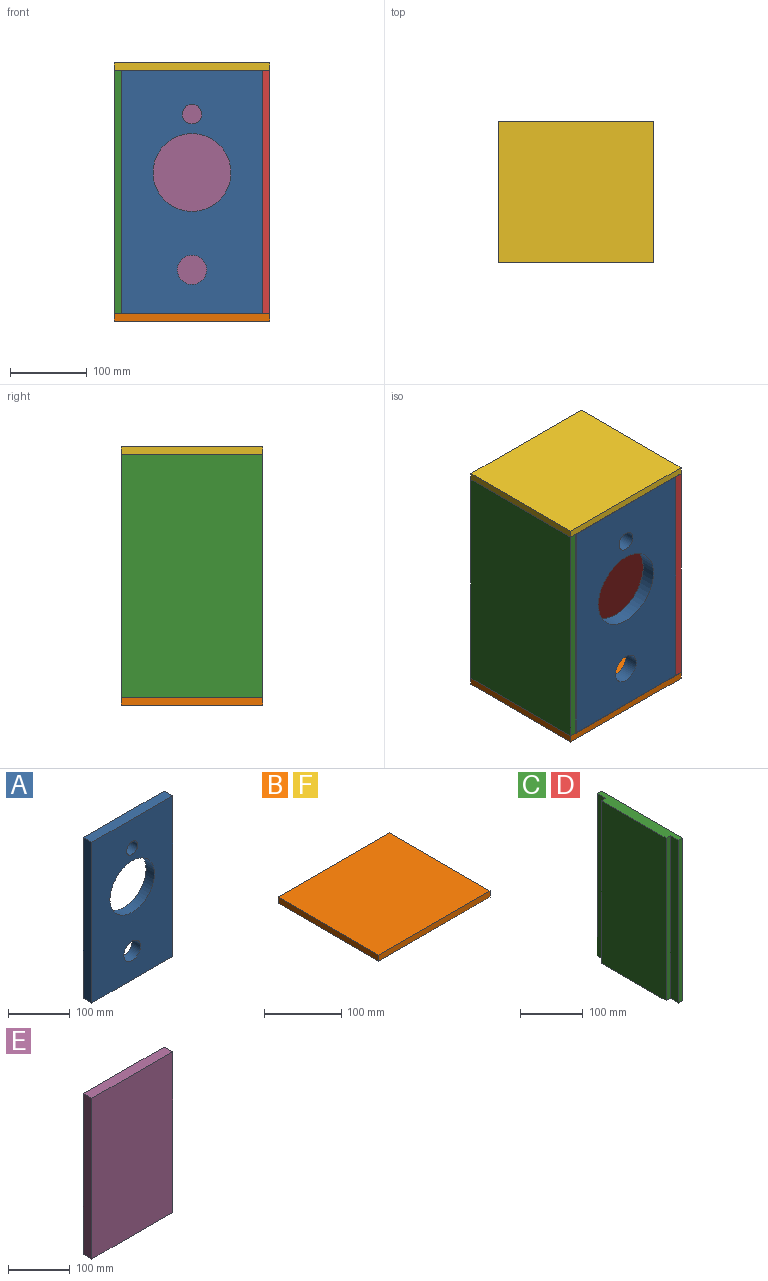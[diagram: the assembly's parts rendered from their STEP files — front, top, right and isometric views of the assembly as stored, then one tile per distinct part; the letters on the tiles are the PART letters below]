
ASSEMBLY  parts=6 mates=5
PART A: 9 faces, bbox 184.2x19.1x317.5 mm
  f0: plane 184.15x19.05mm, normal (0,0,-1), area 3508.1mm2, adj f1,f6,f7,f8
  f1: plane 317.5x19.05mm, normal (1,0,0), area 6048.4mm2, adj f0,f2,f7,f8
  f2: plane 184.15x19.05mm, normal (0,0,1), area 3508.1mm2, adj f1,f6,f7,f8
  f3: cylinder r=50.8mm len=101.6mm, axis (0,1,0), area 6080.5mm2, adj f7,f8
  f4: cylinder r=12.7mm len=25.4mm, axis (0,1,0), area 1520.1mm2, adj f7,f8
  f5: cylinder r=19.05mm len=38.1mm, axis (0,1,0), area 2280.2mm2, adj f7,f8
  f6: plane 317.5x19.05mm, normal (-1,0,0), area 6048.4mm2, adj f0,f2,f7,f8
  f7: plane 317.5x184.15mm, normal (0,-1,0), area 48713.5mm2, adj f0,f1,f2,f3,f4,f5,f6
  f8: plane 317.5x184.15mm, normal (0,1,0), area 48713.5mm2, adj f0,f1,f2,f3,f4,f5,f6
PART B: 11 faces, bbox 203.2x184.2x19.1 mm
  f0: plane 165.1x146.05mm, normal (0,0,-1), area 24112.9mm2, adj f1,f4,f9,f10
  f1: plane 146.05x9.53mm, normal (1,0,0), area 1391.1mm2, adj f0,f8,f9,f10
  f2: plane 203.2x9.53mm, normal (0,-1,0), area 1935.5mm2, adj f5,f6,f7,f8
  f3: plane 203.2x9.53mm, normal (0,1,0), area 1935.5mm2, adj f5,f6,f7,f8
  f4: plane 146.05x9.53mm, normal (-1,0,0), area 1391.1mm2, adj f0,f8,f9,f10
  f5: plane 184.15x9.53mm, normal (1,0,0), area 1754mm2, adj f2,f3,f7,f8
  f6: plane 184.15x9.53mm, normal (-1,0,0), area 1754mm2, adj f2,f3,f7,f8
  f7: plane 203.2x184.15mm, normal (0,0,1), area 37419.3mm2, adj f2,f3,f5,f6
  f8: plane 203.2x184.15mm, normal (0,0,-1), area 13306.4mm2, adj f1,f2,f3,f4,f5,f6,f9,f10
  f9: plane 165.1x9.53mm, normal (0,1,0), area 1572.6mm2, adj f0,f1,f4,f8
  f10: plane 165.1x9.53mm, normal (0,-1,0), area 1572.6mm2, adj f0,f1,f4,f8
PART C: 10 faces, bbox 19.1x184.2x317.5 mm
  f0: plane 317.5x146.05mm, normal (-1,0,0), area 46370.9mm2, adj f1,f3,f6,f8
  f1: plane 184.15x19.05mm, normal (0,0,1), area 3145.2mm2, adj f0,f2,f4,f5,f6,f7,f8,f9
  f2: plane 317.5x9.53mm, normal (0,-1,0), area 3024.2mm2, adj f1,f3,f5,f7
  f3: plane 184.15x19.05mm, normal (0,0,-1), area 3145.2mm2, adj f0,f2,f4,f5,f6,f7,f8,f9
  f4: plane 317.5x9.53mm, normal (0,1,0), area 3024.2mm2, adj f1,f3,f5,f9
  f5: plane 317.5x184.15mm, normal (1,0,0), area 58467.6mm2, adj f1,f2,f3,f4
  f6: plane 317.5x9.53mm, normal (0,-1,0), area 3024.2mm2, adj f0,f1,f3,f7
  f7: plane 317.5x19.05mm, normal (-1,0,0), area 6048.4mm2, adj f1,f2,f3,f6
  f8: plane 317.5x9.53mm, normal (0,1,0), area 3024.2mm2, adj f0,f1,f3,f9
  f9: plane 317.5x19.05mm, normal (-1,0,0), area 6048.4mm2, adj f1,f3,f4,f8
PART D: same geometry as C
PART E: 6 faces, bbox 184.2x19.1x317.5 mm
  f0: plane 184.15x19.05mm, normal (0,0,-1), area 3508.1mm2, adj f1,f3,f4,f5
  f1: plane 317.5x19.05mm, normal (1,0,0), area 6048.4mm2, adj f0,f2,f4,f5
  f2: plane 184.15x19.05mm, normal (0,0,1), area 3508.1mm2, adj f1,f3,f4,f5
  f3: plane 317.5x19.05mm, normal (-1,0,0), area 6048.4mm2, adj f0,f2,f4,f5
  f4: plane 317.5x184.15mm, normal (0,-1,0), area 58467.6mm2, adj f0,f1,f2,f3
  f5: plane 317.5x184.15mm, normal (0,1,0), area 58467.6mm2, adj f0,f1,f2,f3
PART F: same geometry as B
PLACE A at identity fixed
PLACE B rot(axis=(1,0,0),180deg) t=(0,82.55,-158.75)mm
PLACE C rot(axis=(0,0,1),180deg) t=(-92.07,82.55,0)mm
PLACE D t=(92.07,82.55,0)mm
PLACE E rot(axis=(0,0,1),0deg) t=(0,165.1,0)mm
PLACE F t=(0,82.55,158.75)mm
MATE fastened A.f7 <-> B.f3  axis (0,-1,0) through (0,-9.52,-158.75)mm
MATE fastened A.f7 <-> C.f4  axis (0,-1,0) through (-92.07,-9.52,0)mm
MATE fastened A.f7 <-> F.f2  axis (0,-1,0) through (0,-9.52,158.75)mm
MATE fastened E.f5 <-> C.f2  axis (0,1,0) through (-92.08,174.62,0)mm
MATE fastened A.f7 <-> D.f2  axis (0,-1,0) through (92.07,-9.52,0)mm
